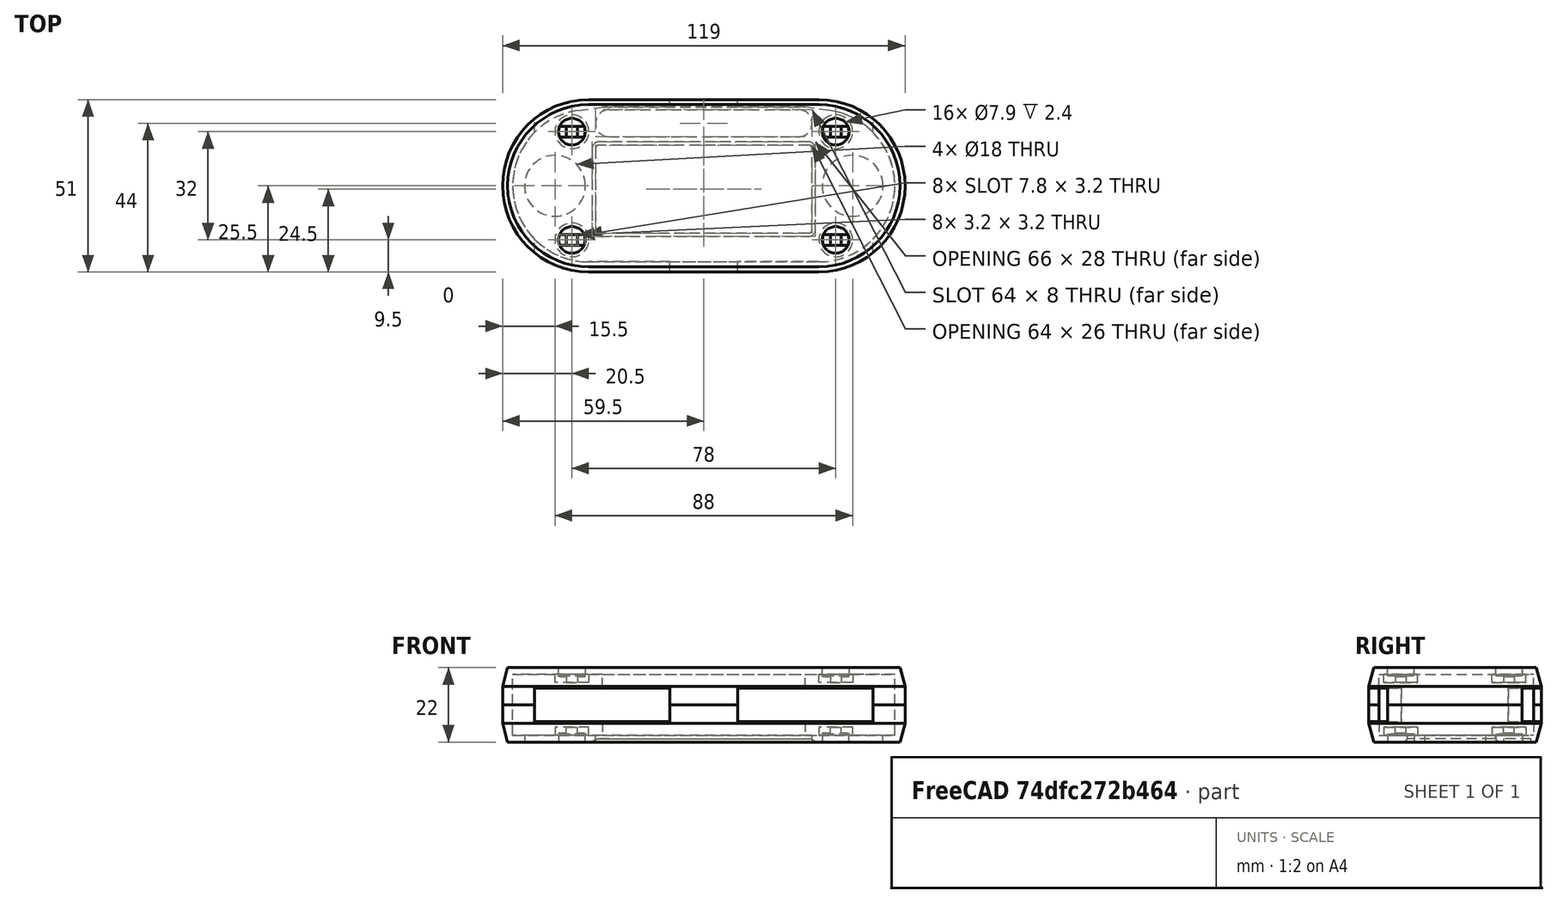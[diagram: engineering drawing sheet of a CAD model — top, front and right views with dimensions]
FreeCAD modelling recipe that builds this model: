
FCSTD DOCUMENT  (FreeCAD 1.0R38641 +678 (Git))
Label: caseB
License: All rights reserved
LicenseURL: https://en.wikipedia.org/wiki/All_rights_reserved
objects: Sketcher::SketchObject×9, PartDesign::Pocket×6, PartDesign::Pad×3, PartDesign::Chamfer×3, Part::FeaturePython×3, Mesh::Feature×2, PartDesign::Plane×1, PartDesign::Mirrored×1, PartDesign::Body×1, App::DocumentObjectGroup×1
note: 61 computed .brp shape members not serialized (recipe doc carries the construction recipe); baked Part::Feature solids carry a one-line shape summary decoded from their .brp

FEATURE [Sketcher::SketchObject] Sketch
  ArcFitTolerance = 0
  AttachmentSupport = -> [XY_Plane]
  FullyConstrained = true
  MakeInternals = false
  MapMode = 5
  sketch-geometry (12):
    g0: LineSegment StartX=-30 StartY=23.2817 StartZ=0 EndX=30 EndY=23.2817 EndZ=0
    g1: LineSegment StartX=-34 StartY=-22.5 StartZ=0 EndX=34 EndY=-22.5 EndZ=0
    g2: LineSegment StartX=30 StartY=23.2817 StartZ=0 EndX=37.1266 EndY=22.2817 EndZ=0
    g3: LineSegment StartX=-30 StartY=23.2817 StartZ=0 EndX=-37.1266 EndY=22.2817 EndZ=0
    g4: ArcOfCircle CenterX=34 CenterY=0 CenterZ=0 NormalX=0 NormalY=0 NormalZ=1 AngleXU=0 Radius=22.5 StartAngle=4.71239 EndAngle=7.71457
    g5: ArcOfCircle CenterX=-34 CenterY=0 CenterZ=0 NormalX=0 NormalY=0 NormalZ=1 AngleXU=0 Radius=22.5 StartAngle=1.71021 EndAngle=4.71239
    g6: LineSegment [constr] StartX=-34 StartY=0 StartZ=0 EndX=34 EndY=0 EndZ=0
    g7: LineSegment [constr] StartX=-37.1266 StartY=22.2817 StartZ=0 EndX=37.1266 EndY=22.2817 EndZ=0
    g8: LineSegment StartX=-34 StartY=25.5 StartZ=0 EndX=34 EndY=25.5 EndZ=0
    g9: LineSegment StartX=34 StartY=-25.5 StartZ=0 EndX=-34 EndY=-25.5 EndZ=0
    g10: ArcOfCircle CenterX=34 CenterY=0 CenterZ=0 NormalX=0 NormalY=0 NormalZ=1 AngleXU=0 Radius=25.5 StartAngle=4.71239 EndAngle=7.85398
    g11: ArcOfCircle CenterX=-34 CenterY=0 CenterZ=0 NormalX=0 NormalY=0 NormalZ=1 AngleXU=0 Radius=25.5 StartAngle=1.5708 EndAngle=4.71239
  constraints (28):
    c: Horizontal(g0)
    c: Horizontal(g1)
    c: Coincident(g3,g0)
    c: Coincident(g2,g0)
    c: Tangent(g5,g1) = -1.5708
    c: Tangent(g1,g4) = -1.5708
    c: Tangent(g4,g2) = 1.5708
    c: Tangent(g3,g5) = -1.5708
    c: Coincident(g5,g6)
    c: Coincident(g6,g4)
    c: Horizontal(g6)
    c: PointOnObject(g-1,g6)
    c: DistanceX(g5,g-1) = 34
    c: DistanceX(g-1,g4) = 34
    c: Radius(g5) = 22.5
    c: Coincident(g7,g2)
    c: Coincident(g3,g7)
    c: DistanceX(g-1,g0) = 30
    c: Horizontal(g7)
    c: DistanceY(g3,g0) = 1
    c: Coincident(g11,g5)
    c: Coincident(g10,g4)
    c: Tangent(g8,g10) = 1.5708
    c: Tangent(g9,g10) = 1.5708
    c: Tangent(g9,g11) = 1.5708
    c: Tangent(g11,g8) = 1.5708
    c: Horizontal(g8)
    c: DistanceY(g9,g1) = 3
FEATURE [PartDesign::Pad] Pad  label="OuterWall"
  Direction = (0,0,1)
  Length = 9
  Length2 = 8.6
  Profile = -> Sketch
  ReferenceAxis = -> Sketch [N_Axis]
  Reversed = true
  Suppressed = false
  Type = 0
FEATURE [Sketcher::SketchObject] Sketch001
  ArcFitTolerance = 0
  AttachmentSupport = -> [Pad]
  FullyConstrained = true
  MakeInternals = false
  MapMode = 5
  Placement = pos=(0,0,-9) rot=(1,0,0;3.14159rad)
  sketch-geometry (5):
    g0: LineSegment StartX=-34 StartY=25.5 StartZ=0 EndX=34 EndY=25.5 EndZ=0
    g1: LineSegment StartX=-34 StartY=-25.5 StartZ=0 EndX=34 EndY=-25.5 EndZ=0
    g2: ArcOfCircle CenterX=34 CenterY=0 CenterZ=0 NormalX=0 NormalY=0 NormalZ=1 AngleXU=0 Radius=25.5 StartAngle=4.71239 EndAngle=7.85398
    g3: ArcOfCircle CenterX=-34 CenterY=0 CenterZ=0 NormalX=0 NormalY=0 NormalZ=1 AngleXU=0 Radius=25.5 StartAngle=1.5708 EndAngle=4.71239
    g4: LineSegment [constr] StartX=-34 StartY=0 StartZ=0 EndX=34 EndY=0 EndZ=0
  constraints (12):
    c: Tangent(g3,g0) = 1.5708
    c: Tangent(g0,g2) = 1.5708
    c: Tangent(g1,g2) = -1.5708
    c: Tangent(g3,g1) = -1.5708
    c: Coincident(g4,g3)
    c: Coincident(g4,g2)
    c: Horizontal(g4)
    c: Equal(g3,g2)
    c: PointOnObject(g-1,g4)
    c: DistanceX(g3,g-1) = 34
    c: DistanceX(g-1,g2) = 34
    c: DistanceY(g2,g0) = 25.5
FEATURE [PartDesign::Pad] Pad001  label="TopPad"
  BaseFeature = -> Pad
  Direction = (0,0,-1)
  Length = 2
  Length2 = 10
  Profile = -> Sketch001
  ReferenceAxis = -> Sketch001 [N_Axis]
  Suppressed = false
  Type = 0
FEATURE [Sketcher::SketchObject] Sketch002
  ArcFitTolerance = 0
  AttachmentSupport = -> [Pad001]
  FullyConstrained = true
  MakeInternals = false
  MapMode = 5
  Placement = pos=(0,0,-11) rot=(1,0,0;3.14159rad)
  sketch-geometry (20):
    g0: LineSegment [constr] StartX=-39 StartY=16 StartZ=0 EndX=39 EndY=16 EndZ=0
    g1: LineSegment [constr] StartX=39 StartY=16 StartZ=0 EndX=39 EndY=-16 EndZ=0
    g2: LineSegment [constr] StartX=39 StartY=-16 StartZ=0 EndX=-39 EndY=-16 EndZ=0
    g3: LineSegment [constr] StartX=-39 StartY=-16 StartZ=0 EndX=-39 EndY=16 EndZ=0
    g4: LineSegment StartX=-40.6 StartY=17.6 StartZ=0 EndX=-40.6 EndY=14.4 EndZ=0
    g5: LineSegment StartX=-40.6 StartY=14.4 StartZ=0 EndX=-37.4 EndY=14.4 EndZ=0
    g6: LineSegment StartX=-37.4 StartY=14.4 StartZ=0 EndX=-37.4 EndY=17.6 EndZ=0
    g7: LineSegment StartX=-37.4 StartY=17.6 StartZ=0 EndX=-40.6 EndY=17.6 EndZ=0
    g8: LineSegment StartX=-40.6 StartY=-14.4 StartZ=0 EndX=-40.6 EndY=-17.6 EndZ=0
    g9: LineSegment StartX=-40.6 StartY=-17.6 StartZ=0 EndX=-37.4 EndY=-17.6 EndZ=0
    g10: LineSegment StartX=-37.4 StartY=-17.6 StartZ=0 EndX=-37.4 EndY=-14.4 EndZ=0
    g11: LineSegment StartX=-37.4 StartY=-14.4 StartZ=0 EndX=-40.6 EndY=-14.4 EndZ=0
    g12: LineSegment StartX=37.4 StartY=17.6 StartZ=0 EndX=37.4 EndY=14.4 EndZ=0
    g13: LineSegment StartX=37.4 StartY=14.4 StartZ=0 EndX=40.6 EndY=14.4 EndZ=0
    g14: LineSegment StartX=40.6 StartY=14.4 StartZ=0 EndX=40.6 EndY=17.6 EndZ=0
    g15: LineSegment StartX=40.6 StartY=17.6 StartZ=0 EndX=37.4 EndY=17.6 EndZ=0
    g16: LineSegment StartX=37.4 StartY=-14.4 StartZ=0 EndX=37.4 EndY=-17.6 EndZ=0
    g17: LineSegment StartX=37.4 StartY=-17.6 StartZ=0 EndX=40.6 EndY=-17.6 EndZ=0
    g18: LineSegment StartX=40.6 StartY=-17.6 StartZ=0 EndX=40.6 EndY=-14.4 EndZ=0
    g19: LineSegment StartX=40.6 StartY=-14.4 StartZ=0 EndX=37.4 EndY=-14.4 EndZ=0
  constraints (60):
    c: Coincident(g0,g1)
    c: Coincident(g1,g2)
    c: Coincident(g2,g3)
    c: Coincident(g3,g0)
    c: Horizontal(g0)
    c: Horizontal(g2)
    c: Vertical(g1)
    c: Vertical(g3)
    c: Distance(g-1,g1) = 39
    c: Distance(g-1,g0) = 16
    c: DistanceX(g2,g2) = 78
    c: DistanceY(g3,g3) = 32
    c: Coincident(g4,g5)
    c: Coincident(g5,g6)
    c: Coincident(g6,g7)
    c: Coincident(g7,g4)
    c: Vertical(g4)
    c: Vertical(g6)
    c: Horizontal(g5)
    c: Horizontal(g7)
    c: DistanceX(g7,g7) = 3.2
    c: Equal(g7,g4)
    c: Distance(g5,g0) = 1.6
    c: Distance(g6,g3) = 1.6
    c: Coincident(g8,g9)
    c: Coincident(g9,g10)
    c: Coincident(g10,g11)
    c: Coincident(g11,g8)
    c: Vertical(g8)
    c: Vertical(g10)
    c: Horizontal(g9)
    c: Horizontal(g11)
    c: Equal(g11,g8)
    c: Equal(g8,g7)
    c: Distance(g10,g3) = 1.6
    c: Distance(g11,g2) = 1.6
    c: Coincident(g12,g13)
    c: Coincident(g13,g14)
    c: Coincident(g14,g15)
    c: Coincident(g15,g12)
    c: Vertical(g12)
    c: Vertical(g14)
    c: Horizontal(g13)
    c: Horizontal(g15)
    c: Equal(g15,g12)
    c: Equal(g12,g7)
    c: Distance(g12,g1) = 1.6
    c: Distance(g0,g15) = 1.6
    c: Coincident(g16,g17)
    c: Coincident(g17,g18)
    c: Coincident(g18,g19)
    c: Coincident(g19,g16)
    c: Vertical(g16)
    c: Vertical(g18)
    c: Horizontal(g17)
    c: Horizontal(g19)
    c: Equal(g19,g16)
    c: Equal(g16,g7)
    c: Distance(g17,g2) = 1.6
    c: Distance(g18,g1) = 1.6
FEATURE [PartDesign::Pocket] Pocket  label="ScrewHoles"
  BaseFeature = -> Pad001
  Direction = (0,0,1)
  Length = 0
  Length2 = 5
  Profile = -> Sketch002
  ReferenceAxis = -> Sketch002 [N_Axis]
  Suppressed = false
  Type = 1
FEATURE [Sketcher::SketchObject] Sketch003
  ArcFitTolerance = 0
  AttachmentSupport = -> [Pocket]
  ExternalGeometry = -> [Pocket]
  FullyConstrained = true
  MakeInternals = false
  MapMode = 5
  Placement = pos=(0,0,-9) rot=(0,0,1;0rad)
  sketch-geometry (20):
    g0: Circle CenterX=-39 CenterY=16 CenterZ=0 NormalX=0 NormalY=0 NormalZ=1 AngleXU=0 Radius=5
    g1: Circle CenterX=-39 CenterY=-16 CenterZ=0 NormalX=0 NormalY=0 NormalZ=1 AngleXU=0 Radius=5
    g2: Circle CenterX=39 CenterY=-16 CenterZ=0 NormalX=0 NormalY=0 NormalZ=1 AngleXU=0 Radius=5
    g3: Circle CenterX=39 CenterY=16 CenterZ=0 NormalX=0 NormalY=0 NormalZ=1 AngleXU=0 Radius=5
    g4: LineSegment StartX=37.4 StartY=17.6 StartZ=0 EndX=40.6 EndY=17.6 EndZ=0
    g5: LineSegment StartX=40.6 StartY=17.6 StartZ=0 EndX=40.6 EndY=14.4 EndZ=0
    g6: LineSegment StartX=40.6 StartY=14.4 StartZ=0 EndX=37.4 EndY=14.4 EndZ=0
    g7: LineSegment StartX=37.4 StartY=17.6 StartZ=0 EndX=37.4 EndY=14.4 EndZ=0
    g8: LineSegment StartX=-40.6 StartY=17.6 StartZ=0 EndX=-37.4 EndY=17.6 EndZ=0
    g9: LineSegment StartX=-37.4 StartY=17.6 StartZ=0 EndX=-37.4 EndY=14.4 EndZ=0
    g10: LineSegment StartX=-37.4 StartY=14.4 StartZ=0 EndX=-40.6 EndY=14.4 EndZ=0
    g11: LineSegment StartX=-40.6 StartY=14.4 StartZ=0 EndX=-40.6 EndY=17.6 EndZ=0
    g12: LineSegment StartX=-40.6 StartY=-14.4 StartZ=0 EndX=-37.4 EndY=-14.4 EndZ=0
    g13: LineSegment StartX=-37.4 StartY=-14.4 StartZ=0 EndX=-37.4 EndY=-17.6 EndZ=0
    g14: LineSegment StartX=-37.4 StartY=-17.6 StartZ=0 EndX=-40.6 EndY=-17.6 EndZ=0
    g15: LineSegment StartX=-40.6 StartY=-17.6 StartZ=0 EndX=-40.6 EndY=-14.4 EndZ=0
    g16: LineSegment StartX=37.4 StartY=-14.4 StartZ=0 EndX=40.6 EndY=-14.4 EndZ=0
    g17: LineSegment StartX=40.6 StartY=-14.4 StartZ=0 EndX=40.6 EndY=-17.6 EndZ=0
    g18: LineSegment StartX=40.6 StartY=-17.6 StartZ=0 EndX=37.4 EndY=-17.6 EndZ=0
    g19: LineSegment StartX=37.4 StartY=-17.6 StartZ=0 EndX=37.4 EndY=-14.4 EndZ=0
  constraints (44):
    c: Equal(g3,g2)
    c: Equal(g2,g1)
    c: Equal(g1,g0)
    c: Coincident(g4,g-16)
    c: Coincident(g4,g-18)
    c: Coincident(g5,g4)
    c: Coincident(g5,g-18)
    c: Coincident(g6,g5)
    c: Coincident(g6,g-17)
    c: Coincident(g7,g4)
    c: Coincident(g7,g6)
    c: Coincident(g8,g-4)
    c: Coincident(g8,g-6)
    c: Coincident(g9,g8)
    c: Coincident(g9,g-6)
    c: Coincident(g10,g9)
    c: Coincident(g10,g-5)
    c: Coincident(g11,g10)
    c: Coincident(g11,g8)
    c: Coincident(g12,g-8)
    c: Coincident(g12,g-9)
    c: Coincident(g13,g12)
    c: Coincident(g13,g-10)
    c: Coincident(g14,g13)
    c: Coincident(g14,g-10)
    c: Coincident(g15,g14)
    c: Coincident(g15,g12)
    c: Coincident(g16,g-12)
    c: Coincident(g16,g-14)
    c: Coincident(g17,g16)
    c: Coincident(g17,g-14)
    c: Coincident(g18,g17)
    c: Coincident(g18,g-13)
    c: Coincident(g19,g18)
    c: Coincident(g19,g16)
    c: Distance(g0,g-2) = 39
    c: Distance(g0,g-1) = 16
    c: Diameter(g0) = 10
    c: Distance(g1,g-1) = 16
    c: Distance(g1,g-2) = 39
    c: Distance(g2,g-2) = 39
    c: Distance(g2,g-1) = 16
    c: Distance(g3,g-1) = 16
    c: DistanceX(g-1,g3) = 39
FEATURE [PartDesign::Pad] Pad002  label="PCBPad"
  BaseFeature = -> Pocket
  Direction = (0,0,1)
  Length = 2.4
  Length2 = 10
  Profile = -> Sketch003
  ReferenceAxis = -> Sketch003 [N_Axis]
  Suppressed = false
  Type = 0
FEATURE [Sketcher::SketchObject] Sketch004
  ArcFitTolerance = 0
  AttachmentSupport = -> [Pad002]
  FullyConstrained = true
  MakeInternals = false
  MapMode = 5
  Placement = pos=(0,0,-11) rot=(1,0,0;3.14159rad)
  sketch-geometry (4):
    g0: Circle CenterX=-39 CenterY=16 CenterZ=0 NormalX=0 NormalY=0 NormalZ=1 AngleXU=0 Radius=3.95
    g1: Circle CenterX=39 CenterY=16 CenterZ=0 NormalX=0 NormalY=0 NormalZ=1 AngleXU=0 Radius=3.95
    g2: Circle CenterX=39 CenterY=-16 CenterZ=0 NormalX=0 NormalY=0 NormalZ=1 AngleXU=0 Radius=3.95
    g3: Circle CenterX=-39 CenterY=-16 CenterZ=0 NormalX=0 NormalY=0 NormalZ=1 AngleXU=0 Radius=3.95
  constraints (8):
    c: Coincident(g0,g-3)
    c: Coincident(g1,g-5)
    c: Coincident(g2,g-6)
    c: Coincident(g3,g-4)
    c: Equal(g0,g1)
    c: Equal(g1,g2)
    c: Equal(g2,g3)
    c: Diameter(g0) = 7.9
FEATURE [PartDesign::Pocket] Pocket001  label="ScrewHeadSocket"
  BaseFeature = -> Pad002
  Direction = (0,0,1)
  Length = 2.4
  Length2 = 5
  Profile = -> Sketch004
  ReferenceAxis = -> Sketch004 [N_Axis]
  Suppressed = false
  Type = 0
FEATURE [PartDesign::Plane] DatumPlane
  AttachmentSupport = -> [XY_Plane]
  Length = 134.454
  MapMode = 2
  ResizeMode = 0
  Width = 66.573
FEATURE [Sketcher::SketchObject] Sketch008
  ArcFitTolerance = 1e-06
  AttachmentSupport = -> [Pocket001]
  ExternalGeometry = -> [Pocket001]
  FullyConstrained = true
  MakeInternals = false
  MapMode = 5
  Placement = pos=(0,0,-8.6) rot=(1,0,0;3.14159rad)
  sketch-geometry (28):
    g0: LineSegment StartX=-42.5567 StartY=14.4 StartZ=0 EndX=-35.4433 EndY=14.4 EndZ=0
    g1: LineSegment [constr] StartX=-35.4433 StartY=14.4 StartZ=0 EndX=-35.4433 EndY=17.6 EndZ=0
    g2: LineSegment StartX=-35.4433 StartY=17.6 StartZ=0 EndX=-42.5567 EndY=17.6 EndZ=0
    g3: LineSegment [constr] StartX=-42.5567 StartY=17.6 StartZ=0 EndX=-42.5567 EndY=14.4 EndZ=0
    g4: GeomPoint [constr] X=-39 Y=16 Z=0
    g5: ArcOfCircle CenterX=-39 CenterY=16 CenterZ=0 NormalX=0 NormalY=0 NormalZ=1 AngleXU=0 Radius=3.9 StartAngle=2.71886 EndAngle=3.56433
    g6: ArcOfCircle CenterX=-39 CenterY=16 CenterZ=0 NormalX=0 NormalY=0 NormalZ=1 AngleXU=0 Radius=3.9 StartAngle=5.86045 EndAngle=6.70592
    g7: LineSegment StartX=35.4433 StartY=14.4 StartZ=0 EndX=42.5567 EndY=14.4 EndZ=0
    g8: LineSegment [constr] StartX=42.5567 StartY=14.4 StartZ=0 EndX=42.5567 EndY=17.6 EndZ=0
    g9: LineSegment StartX=42.5567 StartY=17.6 StartZ=0 EndX=35.4433 EndY=17.6 EndZ=0
    g10: LineSegment [constr] StartX=35.4433 StartY=17.6 StartZ=0 EndX=35.4433 EndY=14.4 EndZ=0
    g11: GeomPoint [constr] X=39 Y=16 Z=0
    g12: ArcOfCircle CenterX=39 CenterY=16 CenterZ=0 NormalX=0 NormalY=0 NormalZ=1 AngleXU=0 Radius=3.9 StartAngle=2.71886 EndAngle=3.56433
    g13: ArcOfCircle CenterX=39 CenterY=16 CenterZ=0 NormalX=0 NormalY=0 NormalZ=1 AngleXU=0 Radius=3.9 StartAngle=5.86045 EndAngle=6.70592
    g14: LineSegment StartX=-42.5567 StartY=-17.6 StartZ=0 EndX=-35.4433 EndY=-17.6 EndZ=0
    g15: LineSegment [constr] StartX=-35.4433 StartY=-17.6 StartZ=0 EndX=-35.4433 EndY=-14.4 EndZ=0
    g16: LineSegment StartX=-35.4433 StartY=-14.4 StartZ=0 EndX=-42.5567 EndY=-14.4 EndZ=0
    g17: LineSegment [constr] StartX=-42.5567 StartY=-14.4 StartZ=0 EndX=-42.5567 EndY=-17.6 EndZ=0
    g18: GeomPoint [constr] X=-39 Y=-16 Z=0
    g19: ArcOfCircle CenterX=-39 CenterY=-16 CenterZ=0 NormalX=0 NormalY=0 NormalZ=1 AngleXU=0 Radius=3.9 StartAngle=2.71886 EndAngle=3.56433
    g20: ArcOfCircle CenterX=-39 CenterY=-16 CenterZ=0 NormalX=0 NormalY=0 NormalZ=1 AngleXU=0 Radius=3.9 StartAngle=5.86045 EndAngle=6.70592
    g21: LineSegment StartX=35.4433 StartY=-17.6 StartZ=0 EndX=42.5567 EndY=-17.6 EndZ=0
    g22: LineSegment [constr] StartX=42.5567 StartY=-17.6 StartZ=0 EndX=42.5567 EndY=-14.4 EndZ=0
    g23: LineSegment StartX=42.5567 StartY=-14.4 StartZ=0 EndX=35.4433 EndY=-14.4 EndZ=0
    g24: LineSegment [constr] StartX=35.4433 StartY=-14.4 StartZ=0 EndX=35.4433 EndY=-17.6 EndZ=0
    g25: GeomPoint [constr] X=39 Y=-16 Z=0
    g26: ArcOfCircle CenterX=39 CenterY=-16 CenterZ=0 NormalX=0 NormalY=0 NormalZ=1 AngleXU=0 Radius=3.9 StartAngle=2.71886 EndAngle=3.56433
    g27: ArcOfCircle CenterX=39 CenterY=-16 CenterZ=0 NormalX=0 NormalY=0 NormalZ=1 AngleXU=0 Radius=3.9 StartAngle=5.86045 EndAngle=6.70592
  constraints (65):
    c: Coincident(g0,g1)
    c: Coincident(g1,g2)
    c: Coincident(g2,g3)
    c: Coincident(g3,g0)
    c: Horizontal(g0)
    c: Horizontal(g2)
    c: Symmetric(g2,g0,g4)
    c: Coincident(g4,g-3)
    c: Coincident(g5,g4)
    c: Coincident(g5,g2)
    c: Coincident(g5,g0)
    c: Coincident(g6,g1)
    c: Coincident(g6,g0)
    c: Coincident(g6,g4)
    c: Distance(g0,g2) = 3.2
    c: Radius(g5) = 3.9
    c: Coincident(g7,g8)
    c: Coincident(g8,g9)
    c: Coincident(g9,g10)
    c: Coincident(g10,g7)
    c: Horizontal(g7)
    c: Horizontal(g9)
    c: Vertical(g10)
    c: Symmetric(g9,g7,g11)
    c: Coincident(g11,g-6)
    c: Coincident(g12,g11)
    c: PointOnObject(g12,g10)
    c: Coincident(g12,g7)
    c: Coincident(g13,g11)
    c: Coincident(g13,g8)
    c: Coincident(g13,g7)
    c: Distance(g7,g9) = 3.2
    c: Radius(g12) = 3.9
    c: Coincident(g14,g15)
    c: Coincident(g15,g16)
    c: Coincident(g16,g17)
    c: Coincident(g17,g14)
    c: Horizontal(g14)
    c: Horizontal(g16)
    c: Symmetric(g16,g14,g18)
    c: Coincident(g18,g-7)
    c: Coincident(g19,g18)
    c: Coincident(g19,g16)
    c: Coincident(g19,g14)
    c: Coincident(g20,g14)
    c: Coincident(g20,g15)
    c: Distance(g17,g17) = 3.2
    c: Radius(g19) = 3.9
    c: Coincident(g20,g18)
    c: Coincident(g21,g22)
    c: Coincident(g22,g23)
    c: Coincident(g23,g24)
    c: Coincident(g24,g21)
    c: Horizontal(g21)
    c: Horizontal(g23)
    c: Symmetric(g23,g21,g25)
    c: Coincident(g25,g-8)
    c: Coincident(g26,g25)
    c: Coincident(g26,g23)
    c: Coincident(g26,g21)
    c: Coincident(g27,g25)
    c: Coincident(g27,g22)
    c: Coincident(g27,g21)
    c: DistanceY(g24,g24) = 3.2
    c: Radius(g26) = 3.9
FEATURE [PartDesign::Pocket] Pocket005  label="SocketOverhang"
  BaseFeature = -> Pocket001
  Direction = (0,0,1)
  Length = 0.2
  Length2 = 5
  Profile = -> Sketch008
  ReferenceAxis = -> Sketch008 [N_Axis]
  Refine = true
  Suppressed = false
  Type = 0
FEATURE [PartDesign::Mirrored] Mirrored
  BaseFeature = -> Pocket005
  MirrorPlane = -> XY_Plane
  Originals = -> [Pad,Pad001,Pocket,Pad002,Pocket001,Pocket005]
  Suppressed = false
  TransformMode = 0
FEATURE [Sketcher::SketchObject] Sketch005
  ArcFitTolerance = 0
  AttachmentSupport = -> [Mirrored]
  FullyConstrained = true
  MakeInternals = false
  MapMode = 5
  Placement = pos=(0,0,-11) rot=(1,0,0;3.14159rad)
  sketch-geometry (10):
    g0: Circle CenterX=-44 CenterY=0 CenterZ=0 NormalX=0 NormalY=0 NormalZ=1 AngleXU=0 Radius=9
    g1: Circle CenterX=44 CenterY=0 CenterZ=0 NormalX=0 NormalY=0 NormalZ=1 AngleXU=0 Radius=9
    g2: LineSegment StartX=-31 StartY=14 StartZ=0 EndX=31 EndY=14 EndZ=0
    g3: LineSegment StartX=-32 StartY=13 StartZ=0 EndX=-32 EndY=-11 EndZ=0
    g4: LineSegment StartX=-31 StartY=-12 StartZ=0 EndX=31 EndY=-12 EndZ=0
    g5: LineSegment StartX=32 StartY=-11 StartZ=0 EndX=32 EndY=13 EndZ=0
    g6: ArcOfCircle CenterX=31 CenterY=13 CenterZ=0 NormalX=0 NormalY=0 NormalZ=1 AngleXU=0 Radius=1 StartAngle=0 EndAngle=1.5708
    g7: ArcOfCircle CenterX=31 CenterY=-11 CenterZ=0 NormalX=0 NormalY=0 NormalZ=1 AngleXU=0 Radius=1 StartAngle=4.71239 EndAngle=6.28319
    g8: ArcOfCircle CenterX=-31 CenterY=-11 CenterZ=0 NormalX=0 NormalY=0 NormalZ=1 AngleXU=0 Radius=1 StartAngle=3.14159 EndAngle=4.71239
    g9: ArcOfCircle CenterX=-31 CenterY=13 CenterZ=0 NormalX=0 NormalY=0 NormalZ=1 AngleXU=0 Radius=1 StartAngle=1.5708 EndAngle=3.14159
  constraints (34):
    c: PointOnObject(g0,g-1)
    c: PointOnObject(g1,g-1)
    c: Equal(g0,g1)
    c: Diameter(g0) = 18
    c: DistanceX(g0,g-1) = 44
    c: DistanceX(g-1,g1) = 44
    c: Horizontal(g2)
    c: Horizontal(g4)
    c: Coincident(g9,g2)
    c: Coincident(g2,g6)
    c: Coincident(g6,g5)
    c: Coincident(g5,g7)
    c: Coincident(g7,g4)
    c: Coincident(g4,g8)
    c: Coincident(g8,g3)
    c: Coincident(g3,g9)
    c: Vertical(g9,g2)
    c: Vertical(g2,g6)
    c: Vertical(g7,g4)
    c: Vertical(g8,g4)
    c: Horizontal(g3,g8)
    c: Horizontal(g3,g9)
    c: Horizontal(g6,g5)
    c: Horizontal(g7,g5)
    c: Vertical(g5)
    c: Vertical(g3)
    c: Equal(g9,g8)
    c: Equal(g8,g7)
    c: Equal(g7,g6)
    c: Radius(g9) = 1
    c: DistanceX(g3,g-1) = 32
    c: DistanceX(g-1,g5) = 32
    c: DistanceY(g-1,g2) = 14
    c: DistanceY(g4,g-1) = 12
FEATURE [PartDesign::Pocket] Pocket002  label="InterfaceHoles"
  BaseFeature = -> Mirrored
  Direction = (0,0,1)
  Length = 0
  Length2 = 5
  Profile = -> Sketch005
  ReferenceAxis = -> Sketch005 [N_Axis]
  Suppressed = false
  Type = 3
  UpToFace = -> DatumPlane [Plane]
FEATURE [Sketcher::SketchObject] Sketch006
  ArcFitTolerance = 0
  AttachmentSupport = -> [Pocket002]
  FullyConstrained = true
  MakeInternals = false
  MapMode = 5
  Placement = pos=(0,-25.5,0) rot=(1,0,0;1.5708rad)
  sketch-geometry (8):
    g0: LineSegment StartX=-50 StartY=5 StartZ=0 EndX=-10 EndY=5 EndZ=0
    g1: LineSegment StartX=-10 StartY=5 StartZ=0 EndX=-10 EndY=-5 EndZ=0
    g2: LineSegment StartX=-10 StartY=-5 StartZ=0 EndX=-50 EndY=-5 EndZ=0
    g3: LineSegment StartX=-50 StartY=-5 StartZ=0 EndX=-50 EndY=5 EndZ=0
    g4: LineSegment StartX=10 StartY=5 StartZ=0 EndX=50 EndY=5 EndZ=0
    g5: LineSegment StartX=50 StartY=5 StartZ=0 EndX=50 EndY=-5 EndZ=0
    g6: LineSegment StartX=50 StartY=-5 StartZ=0 EndX=10 EndY=-5 EndZ=0
    g7: LineSegment StartX=10 StartY=-5 StartZ=0 EndX=10 EndY=5 EndZ=0
  constraints (24):
    c: Coincident(g0,g1)
    c: Coincident(g1,g2)
    c: Coincident(g2,g3)
    c: Coincident(g3,g0)
    c: Horizontal(g0)
    c: Horizontal(g2)
    c: Vertical(g1)
    c: Vertical(g3)
    c: Coincident(g4,g5)
    c: Coincident(g5,g6)
    c: Coincident(g6,g7)
    c: Coincident(g7,g4)
    c: Horizontal(g4)
    c: Horizontal(g6)
    c: Vertical(g5)
    c: Vertical(g7)
    c: Horizontal(g1,g6)
    c: Horizontal(g0,g4)
    c: DistanceX(g1,g-1) = 10
    c: DistanceX(g-1,g6) = 10
    c: DistanceY(g-1,g4) = 5
    c: DistanceY(g1,g-1) = 5
    c: DistanceX(g2,g-1) = 50
    c: DistanceX(g-1,g4) = 50
FEATURE [PartDesign::Pocket] Pocket003  label="PCBVents"
  BaseFeature = -> Pocket002
  Direction = (0,1,-2e-16)
  Length = 0
  Length2 = 5
  Profile = -> Sketch006
  ReferenceAxis = -> Sketch006 [N_Axis]
  Suppressed = false
  Type = 1
FEATURE [Sketcher::SketchObject] Sketch007
  ArcFitTolerance = 0
  AttachmentSupport = -> [Pocket003]
  FullyConstrained = true
  MakeInternals = false
  MapMode = 5
  Placement = pos=(0,0,-11) rot=(1,0,0;3.14159rad)
  sketch-geometry (5):
    g0: LineSegment [constr] StartX=-28 StartY=-18.5 StartZ=0 EndX=28 EndY=-18.5 EndZ=0
    g1: ArcOfCircle CenterX=-28 CenterY=-18.5 CenterZ=0 NormalX=0 NormalY=0 NormalZ=1 AngleXU=0 Radius=4 StartAngle=1.5708 EndAngle=4.71239
    g2: ArcOfCircle CenterX=28 CenterY=-18.5 CenterZ=0 NormalX=0 NormalY=0 NormalZ=1 AngleXU=0 Radius=4 StartAngle=4.71239 EndAngle=7.85398
    g3: LineSegment StartX=-28 StartY=-14.5 StartZ=0 EndX=28 EndY=-14.5 EndZ=0
    g4: LineSegment StartX=-28 StartY=-22.5 StartZ=0 EndX=28 EndY=-22.5 EndZ=0
  constraints (13):
    c: Horizontal(g0)
    c: DistanceX(g-1,g0) = 28
    c: DistanceY(g0,g-1) = 18.5
    c: DistanceX(g0,g-1) = 28
    c: Tangent(g1,g3) = 1.5708
    c: Tangent(g1,g4) = -1.5708
    c: Equal(g1,g2)
    c: Horizontal(g4)
    c: Radius(g2) = 4
    c: Coincident(g1,g0)
    c: Coincident(g0,g2)
    c: Coincident(g4,g2)
    c: Tangent(g3,g2) = 1.5708
FEATURE [PartDesign::Pocket] Pocket004  label="DecorSocket"
  BaseFeature = -> Pocket003
  Direction = (0,0,1)
  Length = 1
  Length2 = 5
  Profile = -> Sketch007
  ReferenceAxis = -> Sketch007 [N_Axis]
  Suppressed = false
  Type = 0
FEATURE [PartDesign::Chamfer] Chamfer  label="ScreenChamfer"
  Angle = 45
  Base = -> Pocket004 [Edge102]
  BaseFeature = -> Pocket004
  ChamferType = 0
  FlipDirection = false
  Refine = true
  Size = 1
  Size2 = 1
  SupportTransform = false
  Suppressed = false
  UseAllEdges = false
FEATURE [PartDesign::Chamfer] Chamfer001  label="TopSideChamfer"
  Angle = 45
  Base = -> Chamfer [Edge103]
  BaseFeature = -> Chamfer
  ChamferType = 1
  FlipDirection = false
  Refine = true
  Size = 1.5
  Size2 = 5.5
  SupportTransform = false
  Suppressed = false
  UseAllEdges = false
FEATURE [PartDesign::Chamfer] Chamfer002  label="BottomSideChamfer"
  Angle = 45
  Base = -> Chamfer001 [Edge76]
  BaseFeature = -> Chamfer001
  ChamferType = 1
  FlipDirection = false
  Refine = true
  Size = 5.5
  Size2 = 1.5
  SupportTransform = false
  Suppressed = false
  UseAllEdges = false
FEATURE [PartDesign::Body] Body
  AllowCompound = false
  Group = -> [Sketch,Pad,Sketch001,Pad001,Sketch002,Pocket,Sketch003,Pad002,Sketch004,Pocket001,Pocket005,Sketch008,Mirrored,Sketch005,Pocket002,Sketch006,Pocket003,Sketch007,Pocket004,DatumPlane,Chamfer,Chamfer001,Chamfer002]
  Origin = -> Origin
  Tip = -> Chamfer002
FEATURE [Part::FeaturePython] Slice  # WARN: FeaturePython — macro-defined, semantics opaque (R4)
  Base = -> Chamfer002
  Mode = 1
  Tolerance = 0
  Tools = -> [DatumPlane]
FEATURE [Part::FeaturePython] Slice_child0  label="Slice.Bottom"  # WARN: FeaturePython — macro-defined, semantics opaque (R4)
  Base = -> Slice
  FilterType = 1
  Invert = false
  OverrideMaxVal = 0
  WindowFrom = 80
  WindowTo = 100
  items = 0
FEATURE [Part::FeaturePython] Slice_child1  label="Slice.Top"  # WARN: FeaturePython — macro-defined, semantics opaque (R4)
  Base = -> Slice
  FilterType = 1
  Invert = false
  OverrideMaxVal = 0
  WindowFrom = 80
  WindowTo = 100
  items = 1
FEATURE [App::DocumentObjectGroup] GrExplode_Slice  label="Exploded Slice"
  Group = -> [Slice_child0,Slice_child1]
FEATURE [Mesh::Feature] Mesh  label="Slice.Bottom (Meshed)"
FEATURE [Mesh::Feature] Mesh001  label="Slice.Top (Meshed)"
